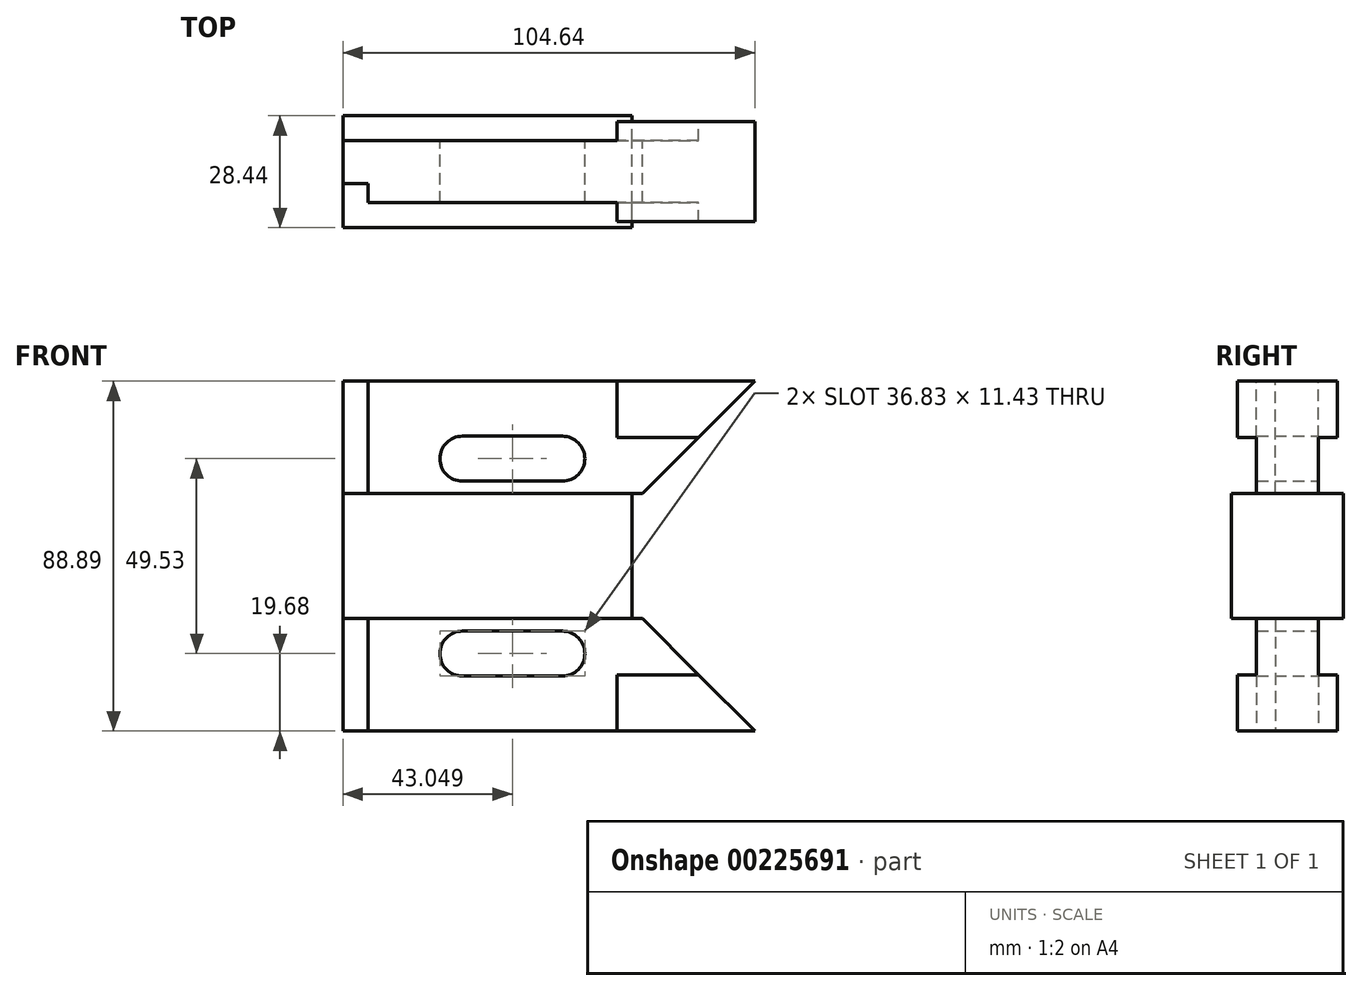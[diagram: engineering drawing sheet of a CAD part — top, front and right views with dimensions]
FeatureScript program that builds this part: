
annotation { "Feature Type Name" : "Feature", "Feature Type Description" : "" }
export const myFeature = defineFeature(function(context is Context, id is Id, definition is map)
    precondition{}
    {
        {
            var Q0;
            Q0=qCreatedBy(makeId("Front.planeOp"),FACE);
            var sketch = newSketch(context, id + "F0", { "sketchPlane" : qUnion([Q0])});
            skLineSegment(sketch, "E0", {"start": v(-52.32, 28.58) * mm, "end": v(-52.32, 0) * mm});
            skLineSegment(sketch, "E1", {"start": v(-52.32, 0) * mm, "end": v(52.32, 0) * mm});
            skLineSegment(sketch, "E2", {"start": v(52.32, 0) * mm, "end": v(52.32, 28.58) * mm});
            skLineSegment(sketch, "E3", {"start": v(52.32, 28.58) * mm, "end": v(-52.32, 28.58) * mm});
            skLineSegment(sketch, "E4", {"start": v(-52.32, 0) * mm, "end": v(-52.32, -15.88) * mm});
            skLineSegment(sketch, "E5", {"start": v(-52.32, -15.87) * mm, "end": v(21.08, -15.87) * mm});
            skLineSegment(sketch, "E6", {"start": v(21.08, -15.87) * mm, "end": v(21.08, 0) * mm});
            skLineSegment(sketch, "E7", {"start": v(-52.32, 0) * mm, "end": v(-45.97, 0) * mm});
            skLineSegment(sketch, "E8", {"start": v(-45.97, 0) * mm, "end": v(-45.97, 28.57) * mm});
            skLineSegment(sketch, "E9", {"start": v(-45.97, 28.58) * mm, "end": v(-52.32, 28.58) * mm});
            skLineSegment(sketch, "E10", {"start": v(52.32, 28.58) * mm, "end": v(52.32, 14.29) * mm});
            skLineSegment(sketch, "E11", {"start": v(52.32, 14.29) * mm, "end": v(17.27, 14.29) * mm});
            skLineSegment(sketch, "E12", {"start": v(17.27, 14.29) * mm, "end": v(17.27, 28.58) * mm});
            skLineSegment(sketch, "E13", {"start": v(23.75, 0) * mm, "end": v(52.32, 28.58) * mm});
            skLineSegment(sketch, "E14", {"start": v(-21.97, 14.6) * mm, "end": v(-21.97, 3.18) * mm});
            skLineSegment(sketch, "E15", {"start": v(-21.97, 3.18) * mm, "end": v(3.43, 3.17) * mm});
            skLineSegment(sketch, "E16", {"start": v(3.43, 3.18) * mm, "end": v(3.43, 14.6) * mm});
            skLineSegment(sketch, "E17", {"start": v(3.43, 14.6) * mm, "end": v(-21.97, 14.6) * mm});
            skArc(sketch, "E18", {"start": v(3.43, 3.17) * mm, "mid": v(9.14, 8.89) * mm, "end": v(3.43, 14.6) * mm});
            skArc(sketch, "E19", {"start": v(3.43, 14.6) * mm, "mid": v(-2.29, 8.9) * mm, "end": v(3.43, 3.17) * mm});
            skArc(sketch, "E20", {"start": v(-21.97, 3.18) * mm, "mid": v(-16.26, 8.9) * mm, "end": v(-21.97, 14.6) * mm});
            skArc(sketch, "E21", {"start": v(-21.97, 14.6) * mm, "mid": v(-27.69, 8.9) * mm, "end": v(-21.97, 3.18) * mm});
            skSolve(sketch);
        }
        {
            var Q0;
            Q0=makeQuery(id+"F0.imprint","IMPRINT",FACE,{"disambiguationData":[TD([[makeQuery(id+"F0.imprint","IMPRINT",EDGE,{"derivedFrom":sQuery(id+"F0.wireOp",EDGE,"E4")}),1.0]])]});
            extrude(context, id + "F1", {"entities" : qUnion([Q0]), "endBound" : BoundingType.SYMMETRIC, "depth" : 28.45 * mm});
        }
        {
            var Q0;
            {var subQ3=sQuery(id+"F0.wireOp",EDGE,"E12");Q0=makeQuery(id+"F0.imprint","IMPRINT",FACE,{"disambiguationData":[TD([[makeQuery(id+"F0.imprint","IMPRINT",EDGE,{"derivedFrom":subQ3}),-1.0]])]});}
            extrude(context, id + "F2", {"entities" : qUnion([Q0]), "endBound" : BoundingType.SYMMETRIC, "depth" : 25.4 * mm});
        }
        {
            var Q0;
            {var subQ4=sQuery(id+"F0.wireOp",EDGE,"E8");Q0=makeQuery(id+"F0.imprint","IMPRINT",FACE,{"disambiguationData":[TD([[makeQuery(id+"F0.imprint","IMPRINT",EDGE,{"derivedFrom":subQ4}),-1.0]])]});}
            extrude(context, id + "F3", {"entities" : qUnion([Q0]), "endBound" : BoundingType.SYMMETRIC, "depth" : 15.75 * mm});
        }
        {
            var Q0;
            Q0=makeQuery(id+"F0.imprint","IMPRINT",FACE,{"disambiguationData":[TD([[makeQuery(id+"F0.imprint","IMPRINT",EDGE,{"derivedFrom":sQuery(id+"F0.wireOp",EDGE,"E0")}),1.0]])]});
            extrude(context, id + "F4", {"entities" : qUnion([Q0]), "oppositeDirection" : true, "depth" : 7.87 * mm});
        }
        {
            var Q0;
            Q0=makeQuery(id+"F0.imprint","IMPRINT",FACE,{"disambiguationData":[TD([[makeQuery(id+"F0.imprint","IMPRINT",EDGE,{"derivedFrom":sQuery(id+"F0.wireOp",EDGE,"E0")}),1.0]])]});
            extrude(context, id + "F5", {"entities" : qUnion([Q0]), "depth" : 3.05 * mm});
        }
        {
            var Q0;
            Q0=makeQuery(id+"F4.opExtrude","SWEPT_BODY",BODY,{"disambiguationData":[OSD([sQuery(id+"F0.wireOp",EDGE,"E0"),sQuery(id+"F0.wireOp",EDGE,"E7"),sQuery(id+"F0.wireOp",EDGE,"E8"),sQuery(id+"F0.wireOp",EDGE,"E9")])]});
            var Q1;
            Q1=makeQuery(id+"F5.opExtrude","SWEPT_BODY",BODY,{"disambiguationData":[OSD([sQuery(id+"F0.wireOp",EDGE,"E0"),sQuery(id+"F0.wireOp",EDGE,"E7"),sQuery(id+"F0.wireOp",EDGE,"E8"),sQuery(id+"F0.wireOp",EDGE,"E9")])]});
            var Q2;
            Q2=makeQuery(id+"F3.opExtrude","SWEPT_BODY",BODY,{"disambiguationData":[OSD([sQuery(id+"F0.wireOp",EDGE,"E1"),sQuery(id+"F0.wireOp",EDGE,"E3"),sQuery(id+"F0.wireOp",EDGE,"E8"),sQuery(id+"F0.wireOp",EDGE,"E11"),sQuery(id+"F0.wireOp",EDGE,"E12"),sQuery(id+"F0.wireOp",EDGE,"E13"),sQuery(id+"F0.wireOp",EDGE,"E15"),sQuery(id+"F0.wireOp",EDGE,"E17"),sQuery(id+"F0.wireOp",EDGE,"E18"),sQuery(id+"F0.wireOp",EDGE,"E21")])]});
            var Q3;
            Q3=makeQuery(id+"F2.opExtrude","SWEPT_BODY",BODY,{"disambiguationData":[OSD([sQuery(id+"F0.wireOp",EDGE,"E3"),sQuery(id+"F0.wireOp",EDGE,"E11"),sQuery(id+"F0.wireOp",EDGE,"E12"),sQuery(id+"F0.wireOp",EDGE,"E13")])]});
            var Q4;
            Q4=makeQuery(id+"F1.opExtrude","SWEPT_BODY",BODY,{"disambiguationData":[OSD([sQuery(id+"F0.wireOp",EDGE,"E1"),sQuery(id+"F0.wireOp",EDGE,"E4"),sQuery(id+"F0.wireOp",EDGE,"E5"),sQuery(id+"F0.wireOp",EDGE,"E6"),sQuery(id+"F0.wireOp",EDGE,"E7")])]});
            var Q5;
            Q5=makeQuery(id+"F1.opExtrude","SWEPT_FACE",FACE,{"disambiguationData":[OSD([sQuery(id+"F0.wireOp",EDGE,"E5")])]});
            mirror(context, id + "F6", {"operationType" : NewBodyOperationType.ADD, "entities" : qUnion([Q0, Q1, Q2, Q3, Q4]), "mirrorPlane" : qUnion([Q5])});
        }
    });
